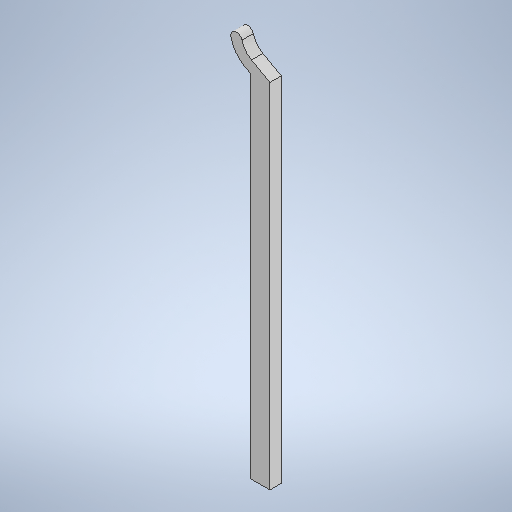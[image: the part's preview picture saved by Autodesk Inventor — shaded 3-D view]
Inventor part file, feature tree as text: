
AUTODESK INVENTOR PART (.ipt)
format: ipt  version: 2025.1 (Build 291241020, 241B)  size: 274,944 bytes
history: native  units: mm
features: extrude x2, sketch x2, fillet x1
ambient origin geometry x8: Origin, YZ Plane, XZ Plane, XY Plane, X Axis, Y Axis, Z Axis, Center Point
bodies: Solid1 (feature_tree)
feature tree (5):
  extrude  "Extrusion1"  Depth=3.0mm TaperAngle=0.0deg
  fillet  "Fillet2"  Radius=10.0mm
  extrude  "Extrusion2"  Depth=3.0mm
  sketch  "Sketch1"  dims[d1=95.0mm d2=3.0mm d3=0.0mm d5=10.0mm]
  sketch  "Sketch3"  dims[d6=3.0mm d7=3.0mm d8=5.0mm d10=1.5mm d12=5.0mm d14=2.1mm d15=0.0mm d16=0.0mm]
